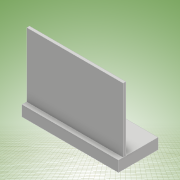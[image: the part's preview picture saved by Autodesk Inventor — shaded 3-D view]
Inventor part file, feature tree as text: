
AUTODESK INVENTOR PART (.ipt)
format: ipt  version: 2017 (Build 210142000, 142)  size: 104,960 bytes
history: native  units: mm
features: extrude x2, sketch x2
ambient origin geometry x8: Origin, YZ Plane, XZ Plane, XY Plane, X Axis, Y Axis, Z Axis, Center Point
bodies: Solid1 (feature_tree)
feature tree (4):
  extrude  "Extrusion1"  Depth=101.6mm TaperAngle=0.0deg
  extrude  "Extrusion2"  [1 undecoded]
  sketch  "Sketch1"  dims[d0=914.4mm d1=101.6mm d2=0.0mm]
  sketch  "Sketch2"  dims[d3=609.6mm d4=0.0mm]
note: 1 required parameter value undecoded (feature->parameter linkage not recoverable at this tier; creation-order binding heuristic only, values carry confidence <= 0.55)
